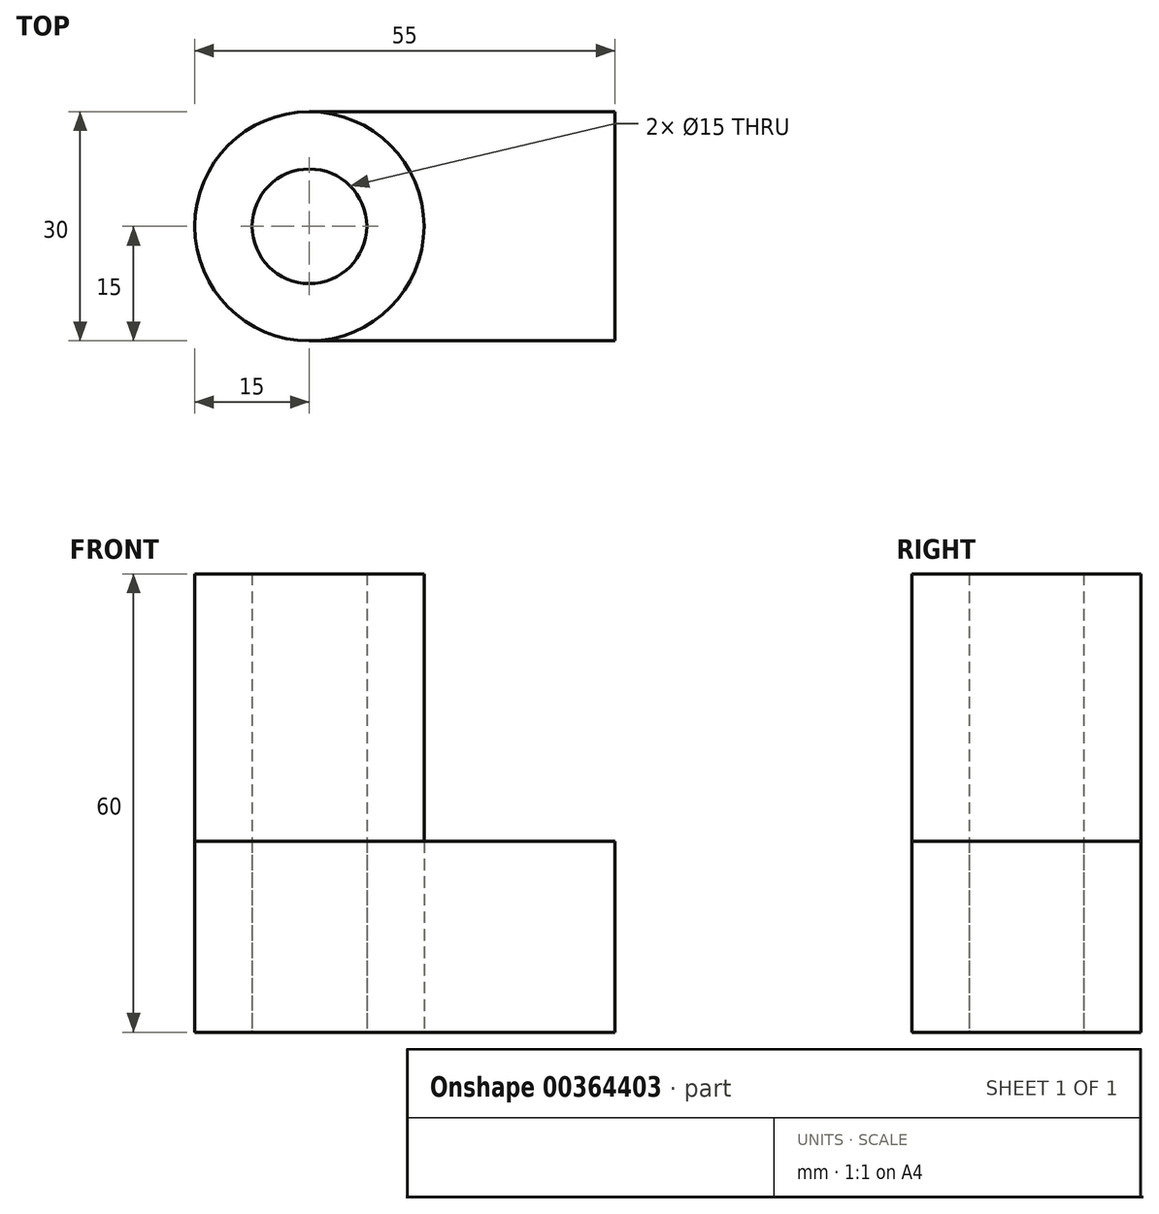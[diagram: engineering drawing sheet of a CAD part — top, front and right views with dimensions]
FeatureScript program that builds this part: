
annotation { "Feature Type Name" : "Feature", "Feature Type Description" : "" }
export const myFeature = defineFeature(function(context is Context, id is Id, definition is map)
    precondition{}
    {
        {
            var Q0;
            Q0=qCreatedBy(makeId("Top.planeOp"),FACE);
            var sketch = newSketch(context, id + "F0", { "sketchPlane" : qUnion([Q0])});
            skLineSegment(sketch, "E0.bottom", {"start": v(0, 0) * mm, "end": v(-40, 0) * mm});
            skLineSegment(sketch, "E0.top", {"start": v(0, 30) * mm, "end": v(-40, 30) * mm});
            skLineSegment(sketch, "E0.left", {"start": v(0, 0) * mm, "end": v(0, 30) * mm});
            skLineSegment(sketch, "E0.right", {"start": v(-40, 0) * mm, "end": v(-40, 30) * mm});
            skCircle(sketch, "E1", {"center": v(-40, 15) * mm, "radius": 15 * mm});
            skCircle(sketch, "E2", {"center": v(-40, 15) * mm, "radius": 7.5 * mm});
            skSolve(sketch);
        }
        {
            var Q0;
            {var subQ1=sQuery(id+"F0.wireOp",EDGE,"E0.right");var subQ3=sQuery(id+"F0.wireOp",EDGE,"E2");var subQ4=makeQuery(id+"F0.imprint","INTERSECT",VERTEX,{"disambiguationData":[OD(0.0)],"derivedFrom":[subQ1,subQ3]});Q0=makeQuery(id+"F0.imprint","IMPRINT",FACE,{"disambiguationData":[TD([[makeQuery(id+"F0.imprint","IMPRINT",EDGE,{"disambiguationData":[TD([[subQ4,1.0]])],"derivedFrom":subQ3}),-1.0]])]});}
            var Q1;
            {var subQ1=sQuery(id+"F0.wireOp",EDGE,"E0.right");var subQ3=sQuery(id+"F0.wireOp",EDGE,"E2");var subQ4=makeQuery(id+"F0.imprint","INTERSECT",VERTEX,{"disambiguationData":[OD(0.0)],"derivedFrom":[subQ1,subQ3]});Q1=makeQuery(id+"F0.imprint","IMPRINT",FACE,{"disambiguationData":[TD([[makeQuery(id+"F0.imprint","IMPRINT",EDGE,{"disambiguationData":[TD([[subQ4,-1.0]])],"derivedFrom":subQ3}),-1.0]])]});}
            extrude(context, id + "F1", {"entities" : qUnion([Q0, Q1]), "depth" : 60 * mm, "offsetDistance" : 25 * mm});
        }
        {
            var Q0;
            {var subQ1=sQuery(id+"F0.wireOp",EDGE,"E0.right");var subQ3=sQuery(id+"F0.wireOp",EDGE,"E2");var subQ4=makeQuery(id+"F0.imprint","INTERSECT",VERTEX,{"disambiguationData":[OD(0.0)],"derivedFrom":[subQ1,subQ3]});Q0=makeQuery(id+"F0.imprint","IMPRINT",FACE,{"disambiguationData":[TD([[makeQuery(id+"F0.imprint","IMPRINT",EDGE,{"disambiguationData":[TD([[subQ4,1.0]])],"derivedFrom":subQ3}),-1.0]])]});}
            var Q1;
            {var subQ1=sQuery(id+"F0.wireOp",EDGE,"E0.right");var subQ3=sQuery(id+"F0.wireOp",EDGE,"E2");var subQ4=makeQuery(id+"F0.imprint","INTERSECT",VERTEX,{"disambiguationData":[OD(0.0)],"derivedFrom":[subQ1,subQ3]});Q1=makeQuery(id+"F0.imprint","IMPRINT",FACE,{"disambiguationData":[TD([[makeQuery(id+"F0.imprint","IMPRINT",EDGE,{"disambiguationData":[TD([[subQ4,-1.0]])],"derivedFrom":subQ3}),-1.0]])]});}
            var Q2;
            {var subQ0=sQuery(id+"F0.wireOp",EDGE,"E0.bottom");Q2=makeQuery(id+"F0.imprint","IMPRINT",FACE,{"disambiguationData":[TD([[makeQuery(id+"F0.imprint","IMPRINT",EDGE,{"derivedFrom":subQ0}),-1.0]])]});}
            extrude(context, id + "F2", {"entities" : qUnion([Q0, Q1, Q2]), "depth" : 25 * mm, "offsetDistance" : 25 * mm});
        }
    });
